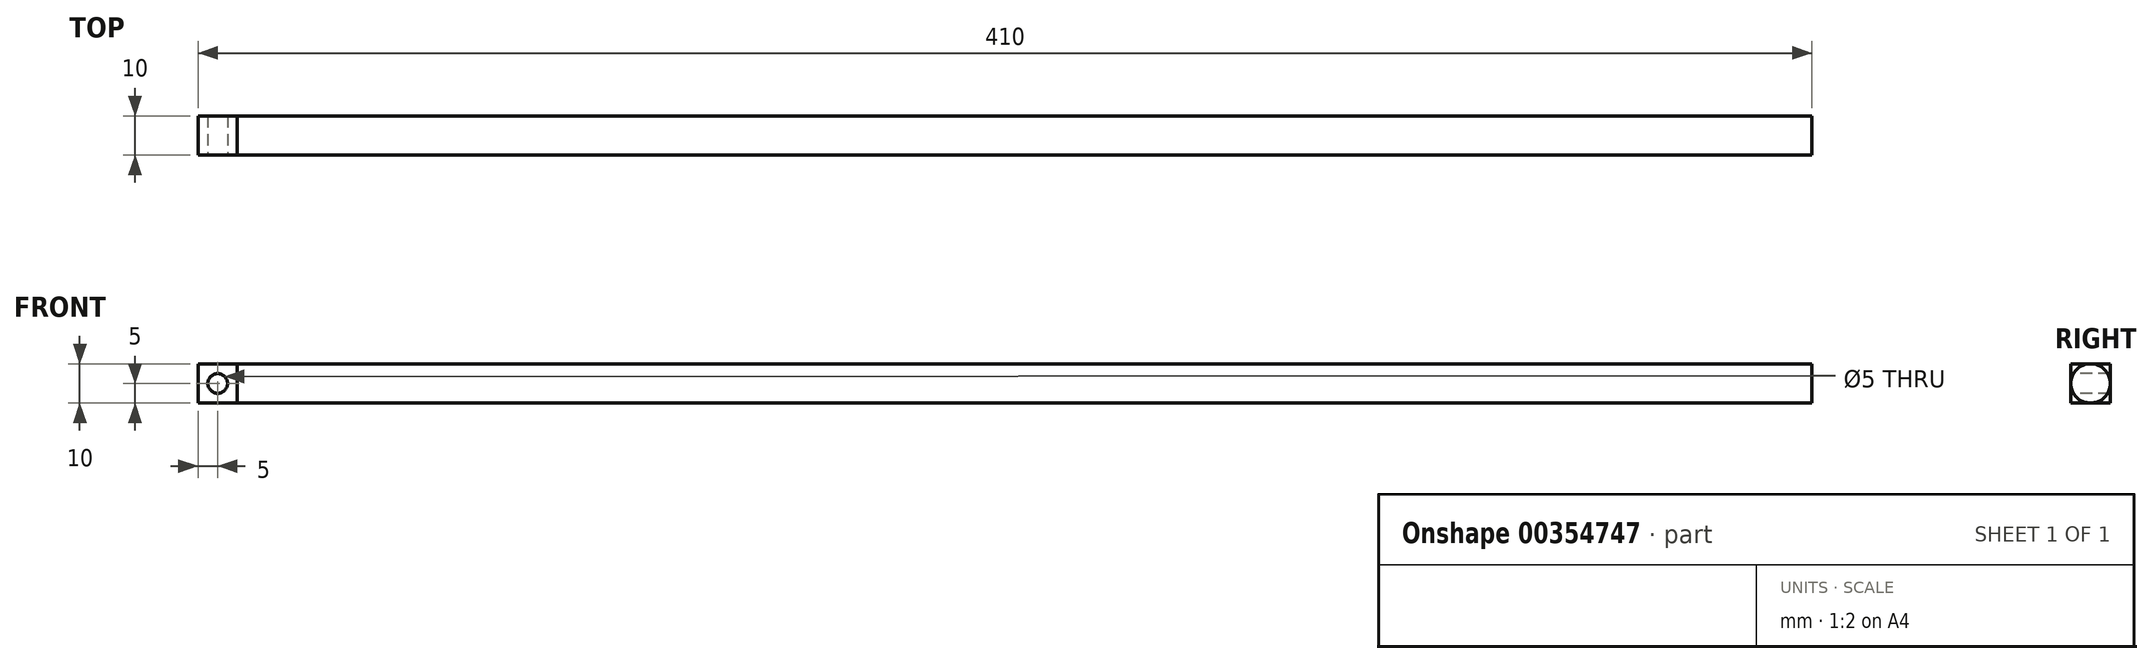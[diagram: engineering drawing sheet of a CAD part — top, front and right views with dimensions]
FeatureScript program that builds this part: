
annotation { "Feature Type Name" : "Feature", "Feature Type Description" : "" }
export const myFeature = defineFeature(function(context is Context, id is Id, definition is map)
    precondition{}
    {
        {
            var Q0;
            Q0=qCreatedBy(makeId("Right.planeOp"),FACE);
            var sketch = newSketch(context, id + "F0", { "sketchPlane" : qUnion([Q0])});
            skCircle(sketch, "E0", {"center": v(0, 0) * mm, "radius": 5 * mm});
            skSolve(sketch);
        }
        {
            var Q0;
            Q0 = qSketchRegion(id + "F0", true);
            extrude(context, id + "F1", {"entities" : qUnion([Q0]), "depth" : 400 * mm});
        }
        {
            var Q0;
            Q0=makeQuery(id+"F1.opExtrude","CAP_FACE",FACE,{"disambiguationData":[OSD([sQuery(id+"F0.wireOp",EDGE,"E0")])],"isStart":true});
            var sketch = newSketch(context, id + "F2", { "sketchPlane" : qUnion([Q0])});
            skLineSegment(sketch, "E1.bottom", {"start": v(5, 5) * mm, "end": v(-5, 5) * mm});
            skLineSegment(sketch, "E1.top", {"start": v(5, -5) * mm, "end": v(-5, -5) * mm});
            skLineSegment(sketch, "E1.left", {"start": v(5, 5) * mm, "end": v(5, -5) * mm});
            skLineSegment(sketch, "E1.right", {"start": v(-5, 5) * mm, "end": v(-5, -5) * mm});
            skPoint(sketch, "E1.middle", {"position": v(0, 0) * mm});
            skSolve(sketch);
        }
        {
            var Q0;
            Q0 = qSketchRegion(id + "F2", true);
            extrude(context, id + "F3", {"entities" : qUnion([Q0]), "operationType" : NewBodyOperationType.ADD, "depth" : 10 * mm});
        }
        {
            var Q0;
            Q0=makeQuery(id+"F3.opExtrude","SWEPT_FACE",FACE,{"disambiguationData":[OSD([sQuery(id+"F2.wireOp",EDGE,"E1.left")])]});
            var sketch = newSketch(context, id + "F4", { "sketchPlane" : qUnion([Q0])});
            skCircle(sketch, "E2", {"center": v(-5, 0) * mm, "radius": 2.5 * mm});
            skPoint(sketch, "E2.centerSnap0", {"position": v(-5, -5) * mm});
            skPoint(sketch, "E2.centerSnap1", {"position": v(-10, 0) * mm});
            skSolve(sketch);
        }
        {
            var Q0;
            Q0 = qSketchRegion(id + "F4", true);
            extrude(context, id + "F5", {"entities" : qUnion([Q0]), "operationType" : NewBodyOperationType.REMOVE, "oppositeDirection" : true, "depth" : 25 * mm});
        }
    });
